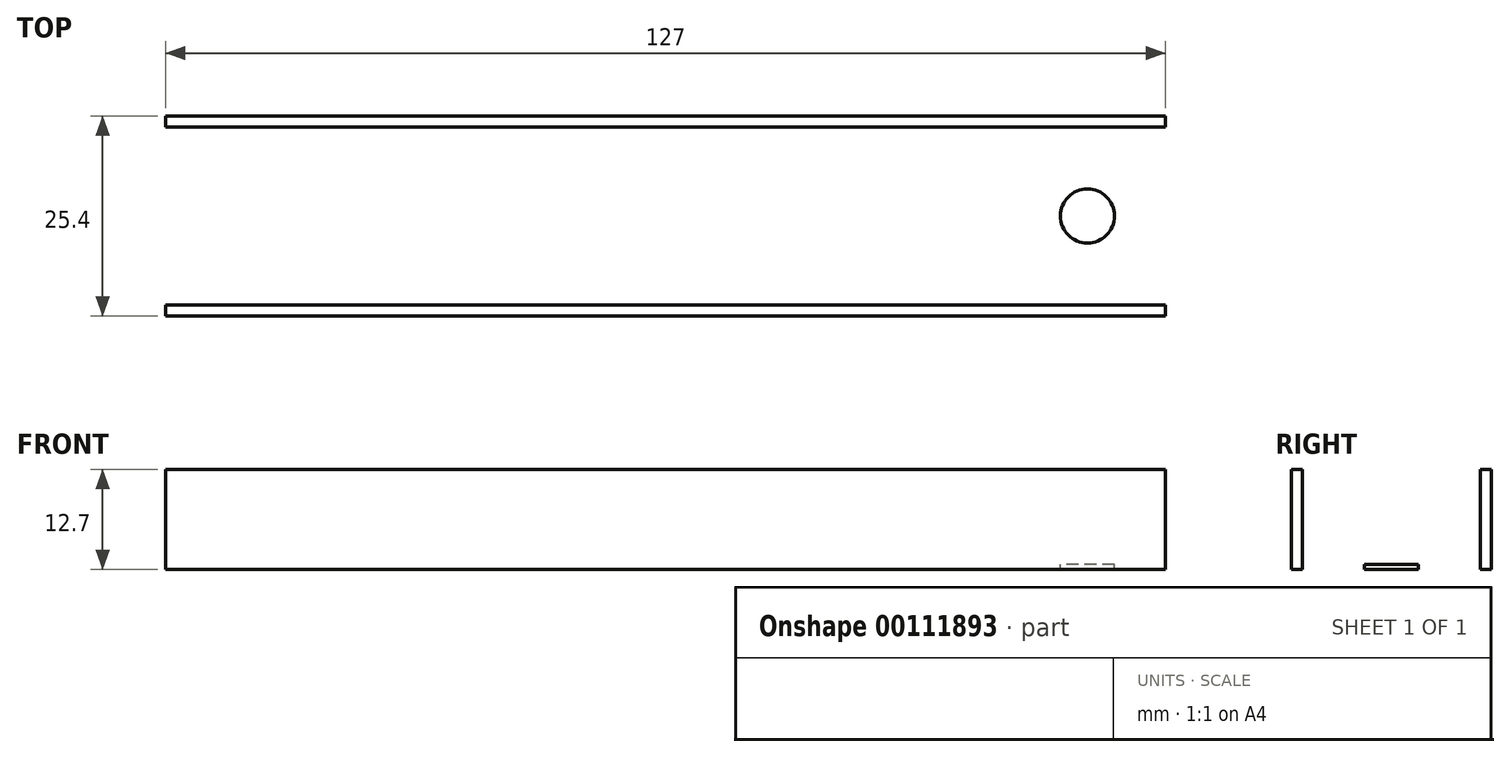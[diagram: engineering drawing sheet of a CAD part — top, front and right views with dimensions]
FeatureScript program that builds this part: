
annotation { "Feature Type Name" : "Feature", "Feature Type Description" : "" }
export const myFeature = defineFeature(function(context is Context, id is Id, definition is map)
    precondition{}
    {
        {
            var Q0;
            Q0=qCreatedBy(makeId("Top.planeOp"),FACE);
            var sketch = newSketch(context, id + "F0", { "sketchPlane" : qUnion([Q0])});
            skLineSegment(sketch, "E0.bottom", {"start": v(63.5, -12.7) * mm, "end": v(-63.5, -12.7) * mm});
            skLineSegment(sketch, "E0.top", {"start": v(63.5, 12.7) * mm, "end": v(-63.5, 12.7) * mm});
            skLineSegment(sketch, "E0.left", {"start": v(63.5, -12.7) * mm, "end": v(63.5, 12.7) * mm});
            skLineSegment(sketch, "E0.right", {"start": v(-63.5, -12.7) * mm, "end": v(-63.5, 12.7) * mm});
            skPoint(sketch, "E0.middle", {"position": v(0, 0) * mm});
            skSolve(sketch);
        }
        {
            var Q0;
            Q0=makeQuery(id+"F0.imprint","IMPRINT",FACE,{"disambiguationData":[TD([[makeQuery(id+"F0.imprint","IMPRINT",EDGE,{"derivedFrom":sQuery(id+"F0.wireOp",EDGE,"E0.bottom")}),-1.0]])]});
            extrude(context, id + "F1", {"entities" : qUnion([Q0]), "depth" : 0.76 * mm});
        }
        {
            var Q0;
            Q0 = qSketchRegion(id + "F0", true);
            extrude(context, id + "F2", {"entities" : qUnion([Q0]), "operationType" : NewBodyOperationType.ADD, "depth" : 12.7 * mm});
        }
        {
            var Q0;
            Q0=qCreatedBy(makeId("Right.planeOp"),FACE);
            var sketch = newSketch(context, id + "F3", { "sketchPlane" : qUnion([Q0])});
            skLineSegment(sketch, "E1.bottom", {"start": v(11.29, 0.61) * mm, "end": v(-11.29, 0.61) * mm});
            skLineSegment(sketch, "E1.top", {"start": v(11.29, 24.8) * mm, "end": v(-11.29, 24.8) * mm});
            skLineSegment(sketch, "E1.left", {"start": v(11.29, 0.61) * mm, "end": v(11.29, 24.8) * mm});
            skLineSegment(sketch, "E1.right", {"start": v(-11.29, 0.61) * mm, "end": v(-11.29, 24.8) * mm});
            skPoint(sketch, "E1.middle", {"position": v(0, 12.7) * mm});
            skSolve(sketch);
        }
        {
            var Q0;
            Q0 = qSketchRegion(id + "F3", true);
            extrude(context, id + "F4", {"entities" : qUnion([Q0]), "operationType" : NewBodyOperationType.REMOVE, "oppositeDirection" : true, "depth" : 101.6 * mm, "hasSecondDirection" : true, "secondDirectionOppositeDirection" : false, "secondDirectionDepth" : 101.6 * mm});
        }
        {
            var Q0;
            Q0=makeQuery(id+"F4.boolean.opBoolean","COPY",FACE,{"derivedFrom":makeQuery(id+"F4.opExtrude","SWEPT_FACE",FACE,{"disambiguationData":[OSD([sQuery(id+"F3.wireOp",EDGE,"E1.bottom")])]})});
            var sketch = newSketch(context, id + "F5", { "sketchPlane" : qUnion([Q0])});
            skCircle(sketch, "E2", {"center": v(-53.6, 0) * mm, "radius": 3.43 * mm});
            skPoint(sketch, "E2.centerSnap0", {"position": v(-63.5, 0) * mm});
            skArc(sketch, "E3", {"start": v(-35.81, 3.43) * mm, "mid": v(-39.24, 0) * mm, "end": v(-35.81, -3.43) * mm});
            skArc(sketch, "E4", {"start": v(-22.48, -3.43) * mm, "mid": v(-19.05, 0) * mm, "end": v(-22.48, 3.43) * mm});
            skCircle(sketch, "E5", {"center": v(0, 0) * mm, "radius": 3.43 * mm});
            skLineSegment(sketch, "E6", {"start": v(-35.81, 3.43) * mm, "end": v(-22.48, 3.43) * mm});
            skLineSegment(sketch, "E7", {"start": v(-35.81, -3.43) * mm, "end": v(-22.48, -3.43) * mm});
            skLineSegment(sketch, "E8.MirrorCS", {"start": v(35.81, 3.43) * mm, "end": v(22.48, 3.43) * mm});
            skLineSegment(sketch, "E9.MirrorCS", {"start": v(35.81, -3.43) * mm, "end": v(22.48, -3.43) * mm});
            skArc(sketch, "E10.MirrorCS", {"start": v(35.81, 3.43) * mm, "mid": v(39.24, 0) * mm, "end": v(35.81, -3.43) * mm});
            skArc(sketch, "E11.MirrorCS", {"start": v(22.48, -3.43) * mm, "mid": v(19.05, 0) * mm, "end": v(22.48, 3.43) * mm});
            skCircle(sketch, "E12.MirrorC", {"center": v(53.6, 0) * mm, "radius": 3.43 * mm});
            skSolve(sketch);
        }
        {
            var Q0;
            Q0=makeQuery(id+"F5.imprint","IMPRINT",FACE,{"disambiguationData":[TD([[makeQuery(id+"F5.imprint","IMPRINT",EDGE,{"derivedFrom":sQuery(id+"F5.wireOp",EDGE,"E5")}),1.0]])]});
            var Q1;
            Q1=makeQuery(id+"F5.imprint","IMPRINT",FACE,{"disambiguationData":[TD([[makeQuery(id+"F5.imprint","IMPRINT",EDGE,{"derivedFrom":sQuery(id+"F5.wireOp",EDGE,"E2")}),1.0]])]});
            var Q2;
            Q2=makeQuery(id+"F5.imprint","IMPRINT",FACE,{"disambiguationData":[TD([[makeQuery(id+"F5.imprint","IMPRINT",EDGE,{"derivedFrom":sQuery(id+"F5.wireOp",EDGE,"E3")}),1.0]])]});
            var Q3;
            Q3=makeQuery(id+"F5.imprint","IMPRINT",FACE,{"disambiguationData":[TD([[makeQuery(id+"F5.imprint","IMPRINT",EDGE,{"derivedFrom":sQuery(id+"F5.wireOp",EDGE,"E8.MirrorCS")}),1.0]])]});
            var Q4;
            Q4=makeQuery(id+"F5.imprint","IMPRINT",FACE,{"disambiguationData":[TD([[makeQuery(id+"F5.imprint","IMPRINT",EDGE,{"derivedFrom":sQuery(id+"F5.wireOp",EDGE,"E12.MirrorC")}),-1.0]])]});
            extrude(context, id + "F6", {"entities" : qUnion([Q0, Q1, Q2, Q3, Q4]), "operationType" : NewBodyOperationType.REMOVE, "oppositeDirection" : true, "depth" : 25.4 * mm});
        }
    });
